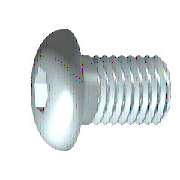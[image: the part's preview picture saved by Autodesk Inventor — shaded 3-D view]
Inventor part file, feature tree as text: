
AUTODESK INVENTOR PART (.ipt)
format: ipt  version: 2024.2 (Build 282272000, 272)  size: 202,240 bytes
history: native  units: mm (DEFAULTED — no unit token found)
features: extrude x1, plane x1, fillet x1
ambient origin geometry x7: Origin, YZ Plane, XY Plane, X Axis, Y Axis, Z Axis, Center Point
bodies: Solid1 (feature_tree), Body (feature_tree)
feature tree (3):
  extrude  "Slot"  Depth=7.0mm
  plane  "Work Plane1"
  fillet  "Fillet2"  Radius=0.61355mm
